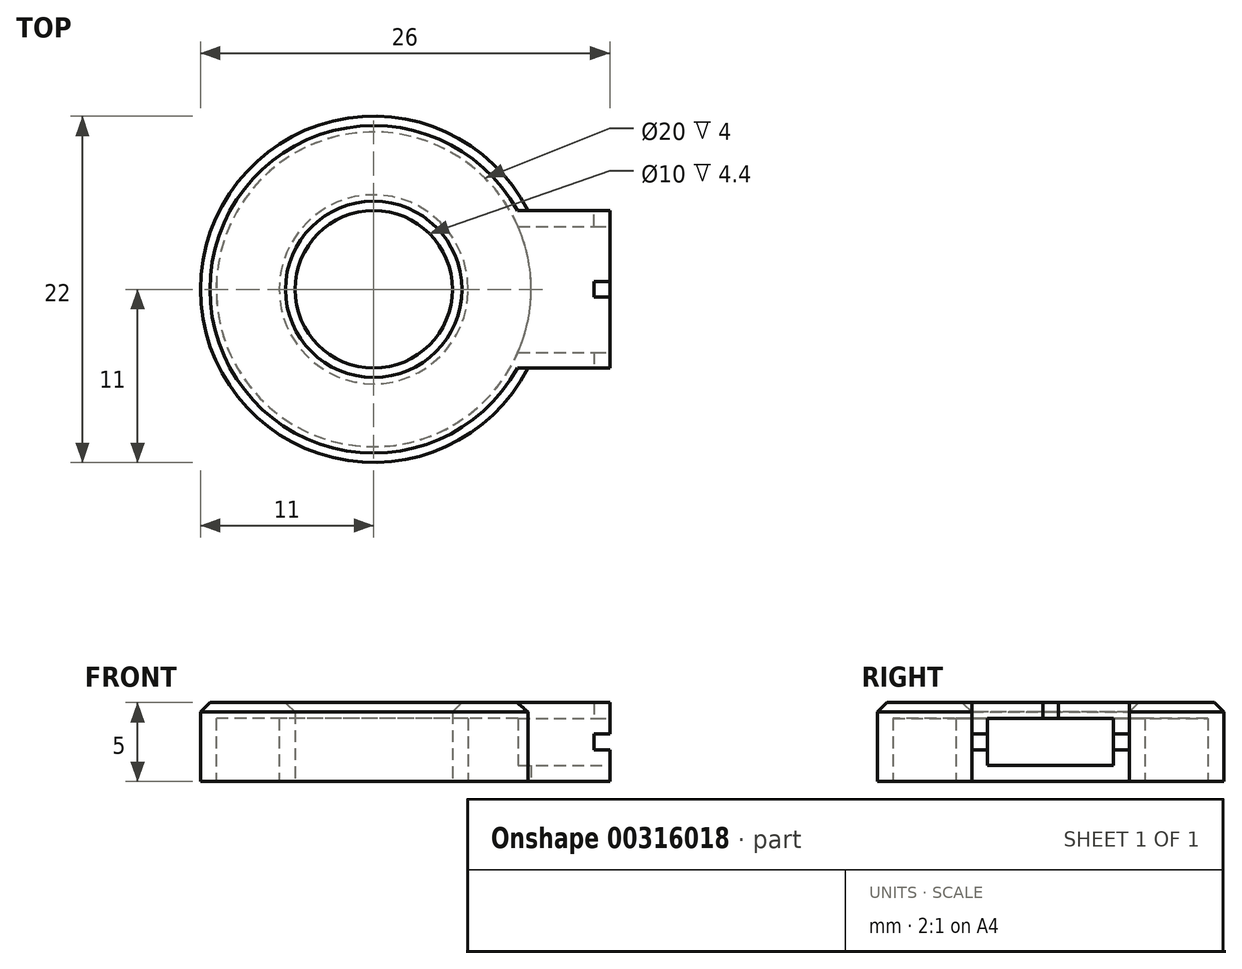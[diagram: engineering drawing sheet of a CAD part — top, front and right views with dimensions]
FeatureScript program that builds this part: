
annotation { "Feature Type Name" : "Feature", "Feature Type Description" : "" }
export const myFeature = defineFeature(function(context is Context, id is Id, definition is map)
    precondition{}
    {
        {
            var Q0;
            Q0=qCreatedBy(makeId("Top.planeOp"),FACE);
            var sketch = newSketch(context, id + "F0", { "sketchPlane" : qUnion([Q0])});
            skCircle(sketch, "E0", {"center": v(0, 0) * mm, "radius": 5 * mm});
            skCircle(sketch, "E1", {"center": v(0, 0) * mm, "radius": 11 * mm});
            skLineSegment(sketch, "E2.bottom", {"start": v(0, 5) * mm, "end": v(15, 5) * mm});
            skLineSegment(sketch, "E2.top", {"start": v(0, -5) * mm, "end": v(15, -5) * mm});
            skLineSegment(sketch, "E2.left", {"start": v(0, 5) * mm, "end": v(0, -5) * mm});
            skLineSegment(sketch, "E2.right", {"start": v(15, 5) * mm, "end": v(15, -5) * mm});
            skSolve(sketch);
        }
        {
            var Q0;
            {var subQ1=sQuery(id+"F0.wireOp",EDGE,"E2.bottom");var subQ6=sQuery(id+"F0.wireOp",EDGE,"E1");var subQ7=makeQuery(id+"F0.imprint","INTERSECT",VERTEX,{"derivedFrom":[subQ6,subQ1]});Q0=makeQuery(id+"F0.imprint","IMPRINT",FACE,{"disambiguationData":[TD([[makeQuery(id+"F0.imprint","IMPRINT",EDGE,{"disambiguationData":[TD([[subQ7,-1.0]])],"derivedFrom":subQ6}),1.0]])]});}
            var Q1;
            {var subQ1=sQuery(id+"F0.wireOp",EDGE,"E2.bottom");var subQ6=sQuery(id+"F0.wireOp",EDGE,"E1");var subQ8=makeQuery(id+"F0.imprint","INTERSECT",VERTEX,{"derivedFrom":[subQ6,subQ1]});Q1=makeQuery(id+"F0.imprint","IMPRINT",FACE,{"disambiguationData":[TD([[makeQuery(id+"F0.imprint","IMPRINT",EDGE,{"disambiguationData":[TD([[subQ8,1.0]])],"derivedFrom":subQ6}),1.0]])]});}
            extrude(context, id + "F1", {"entities" : qUnion([Q0, Q1]), "depth" : 5 * mm});
        }
        {
            var Q0;
            Q0=makeQuery(id+"F1.opExtrude","CAP_FACE",FACE,{"disambiguationData":[OSD([sQuery(id+"F0.wireOp",EDGE,"E0"),sQuery(id+"F0.wireOp",EDGE,"E1")])],"isStart":true});
            shell(context, id + "F2", {"entities" : qUnion([Q0]), "thickness" : 1 * mm});
        }
        {
            var Q0;
            {var subQ5=sQuery(id+"F0.wireOp",EDGE,"E2.right");Q0=makeQuery(id+"F0.imprint","IMPRINT",FACE,{"disambiguationData":[TD([[makeQuery(id+"F0.imprint","IMPRINT",EDGE,{"derivedFrom":subQ5}),-1.0]])]});}
            extrude(context, id + "F3", {"entities" : qUnion([Q0]), "operationType" : NewBodyOperationType.ADD, "depth" : 5 * mm});
        }
        {
            var Q0;
            Q0=makeQuery(id+"F3.opExtrude","SWEPT_FACE",FACE,{"disambiguationData":[OSD([sQuery(id+"F0.wireOp",EDGE,"E2.right")])]});
            var sketch = newSketch(context, id + "F4", { "sketchPlane" : qUnion([Q0])});
            skLineSegment(sketch, "E3.0", {"start": v(-4, 1) * mm, "end": v(4, 1) * mm});
            skLineSegment(sketch, "E3.1", {"start": v(-4, 4) * mm, "end": v(-4, 1) * mm});
            skLineSegment(sketch, "E3.2", {"start": v(4, 4) * mm, "end": v(-4, 4) * mm});
            skLineSegment(sketch, "E3.3", {"start": v(4, 1) * mm, "end": v(4, 4) * mm});
            skLineSegment(sketch, "E4.bottom", {"start": v(-0.5, 5) * mm, "end": v(0.5, 5) * mm});
            skLineSegment(sketch, "E4.top", {"start": v(-0.5, 4) * mm, "end": v(0.5, 4) * mm});
            skLineSegment(sketch, "E4.left", {"start": v(-0.5, 5) * mm, "end": v(-0.5, 4) * mm});
            skLineSegment(sketch, "E4.right", {"start": v(0.5, 5) * mm, "end": v(0.5, 4) * mm});
            skPoint(sketch, "E5", {"position": v(0, 4) * mm});
            skPoint(sketch, "E6", {"position": v(-4, 2.5) * mm});
            skPoint(sketch, "E7", {"position": v(0, 1) * mm});
            skPoint(sketch, "E8", {"position": v(4, 2.5) * mm});
            skLineSegment(sketch, "E9.bottom", {"start": v(-4, 3) * mm, "end": v(-5, 3) * mm});
            skLineSegment(sketch, "E9.top", {"start": v(-4, 2) * mm, "end": v(-5, 2) * mm});
            skLineSegment(sketch, "E9.left", {"start": v(-4, 3) * mm, "end": v(-4, 2) * mm});
            skLineSegment(sketch, "E9.right", {"start": v(-5, 3) * mm, "end": v(-5, 2) * mm});
            skLineSegment(sketch, "E10.bottom", {"start": v(4, 3) * mm, "end": v(5, 3) * mm});
            skLineSegment(sketch, "E10.top", {"start": v(4, 2) * mm, "end": v(5, 2) * mm});
            skLineSegment(sketch, "E10.left", {"start": v(4, 3) * mm, "end": v(4, 2) * mm});
            skLineSegment(sketch, "E10.right", {"start": v(5, 3) * mm, "end": v(5, 2) * mm});
            skLineSegment(sketch, "E11.bottom", {"start": v(-0.5, 1) * mm, "end": v(0.5, 1) * mm});
            skLineSegment(sketch, "E11.top", {"start": v(-0.5, 0) * mm, "end": v(0.5, 0) * mm});
            skLineSegment(sketch, "E11.left", {"start": v(-0.5, 1) * mm, "end": v(-0.5, 0) * mm});
            skLineSegment(sketch, "E11.right", {"start": v(0.5, 1) * mm, "end": v(0.5, 0) * mm});
            skSolve(sketch);
        }
        {
            var Q0;
            Q0=makeQuery(id+"F4.imprint","IMPRINT",FACE,{"disambiguationData":[TD([[makeQuery(id+"F4.imprint","IMPRINT",EDGE,{"derivedFrom":sQuery(id+"F4.wireOp",EDGE,"E3.0")}),1.0]])]});
            extrude(context, id + "F5", {"entities" : qUnion([Q0]), "operationType" : NewBodyOperationType.REMOVE, "endBound" : BoundingType.UP_TO_NEXT, "oppositeDirection" : true, "depth" : 25 * mm});
        }
        {
            var Q0;
            Q0=makeQuery(id+"F1.opExtrude","CAP_EDGE",EDGE,{"disambiguationData":[OSD([sQuery(id+"F0.wireOp",EDGE,"E1")])],"isStart":false});
            var Q1;
            Q1=makeQuery(id+"F1.opExtrude","CAP_EDGE",EDGE,{"disambiguationData":[OSD([sQuery(id+"F0.wireOp",EDGE,"E0")])],"isStart":false});
            chamfer(context, id + "F6", {"entities" : qUnion([Q0, Q1]), "width" : 0.6 * mm, "tangentPropagation" : true});
        }
        {
            var Q0;
            Q0=makeQuery(id+"F4.imprint","IMPRINT",FACE,{"disambiguationData":[TD([[makeQuery(id+"F4.imprint","IMPRINT",EDGE,{"derivedFrom":sQuery(id+"F4.wireOp",EDGE,"E4.bottom")}),1.0]])]});
            var Q1;
            Q1=makeQuery(id+"F4.imprint","IMPRINT",FACE,{"disambiguationData":[TD([[makeQuery(id+"F4.imprint","IMPRINT",EDGE,{"derivedFrom":sQuery(id+"F4.wireOp",EDGE,"E9.bottom")}),1.0]])]});
            var Q2;
            Q2=makeQuery(id+"F4.imprint","IMPRINT",FACE,{"disambiguationData":[TD([[makeQuery(id+"F4.imprint","IMPRINT",EDGE,{"derivedFrom":sQuery(id+"F4.wireOp",EDGE,"E11.bottom")}),-1.0]])]});
            var Q3;
            Q3=makeQuery(id+"F4.imprint","IMPRINT",FACE,{"disambiguationData":[TD([[makeQuery(id+"F4.imprint","IMPRINT",EDGE,{"derivedFrom":sQuery(id+"F4.wireOp",EDGE,"E10.bottom")}),-1.0]])]});
            extrude(context, id + "F7", {"entities" : qUnion([Q0, Q1, Q2, Q3]), "operationType" : NewBodyOperationType.REMOVE, "oppositeDirection" : true, "depth" : 1 * mm});
        }
    });
